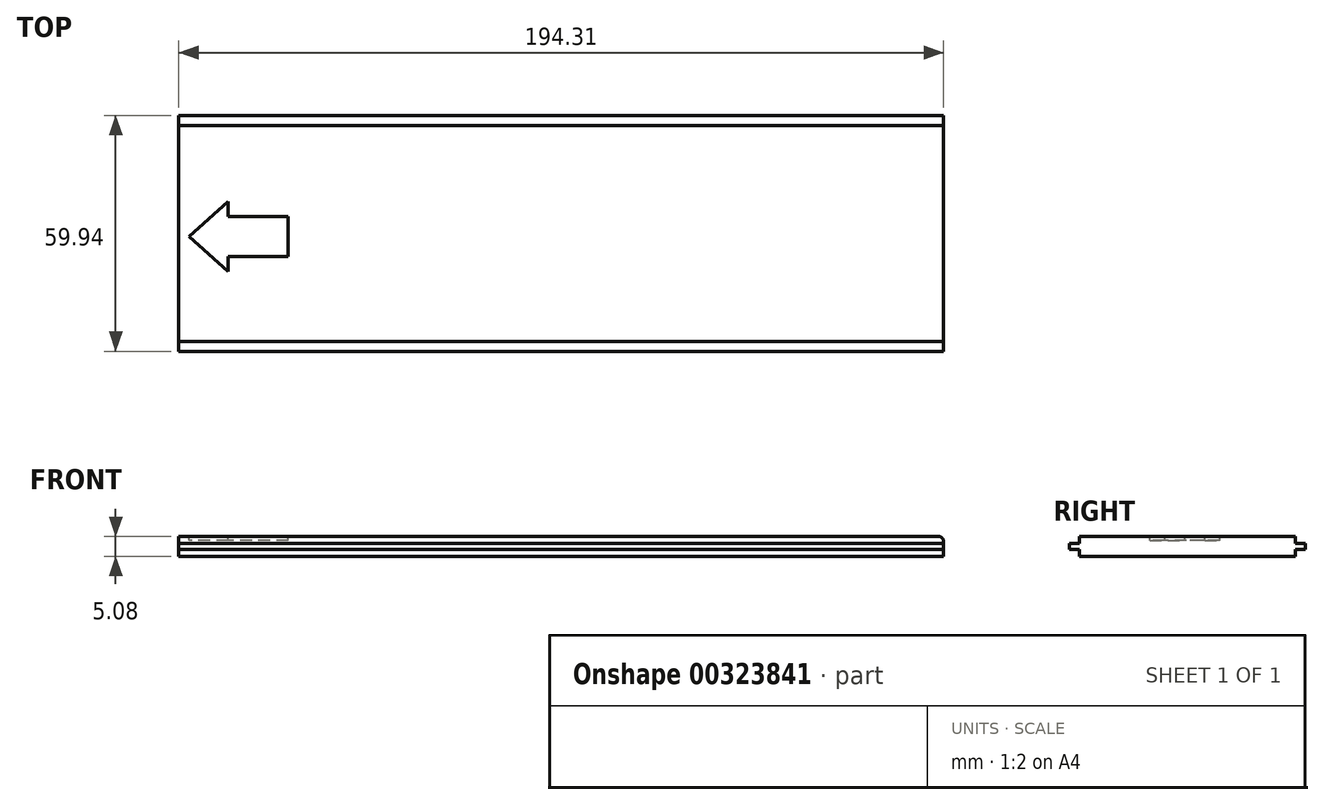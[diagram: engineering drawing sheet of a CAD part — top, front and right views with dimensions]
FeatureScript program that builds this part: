
annotation { "Feature Type Name" : "Feature", "Feature Type Description" : "" }
export const myFeature = defineFeature(function(context is Context, id is Id, definition is map)
    precondition{}
    {
        {
            var Q0;
            Q0=qCreatedBy(makeId("Top.planeOp"),FACE);
            var sketch = newSketch(context, id + "F0", { "sketchPlane" : qUnion([Q0])});
            skLineSegment(sketch, "E0.bottom", {"start": v(-32.03, -26.71) * mm, "end": v(162.28, -26.71) * mm});
            skLineSegment(sketch, "E0.top", {"start": v(-32.03, 28.15) * mm, "end": v(162.28, 28.15) * mm});
            skLineSegment(sketch, "E0.left", {"start": v(-32.03, -26.71) * mm, "end": v(-32.03, 28.15) * mm});
            skLineSegment(sketch, "E0.right", {"start": v(162.28, -26.71) * mm, "end": v(162.28, 28.15) * mm});
            skSolve(sketch);
        }
        {
            var Q0;
            Q0=makeQuery(id+"F0.imprint","IMPRINT",FACE,{"disambiguationData":[TD([[makeQuery(id+"F0.imprint","IMPRINT",EDGE,{"derivedFrom":sQuery(id+"F0.wireOp",EDGE,"E0.bottom")}),1.0]])]});
            extrude(context, id + "F1", {"entities" : qUnion([Q0]), "depth" : 5.08 * mm});
        }
        {
            var Q0;
            Q0=makeQuery(id+"F1.opExtrude","SWEPT_FACE",FACE,{"disambiguationData":[OSD([sQuery(id+"F0.wireOp",EDGE,"E0.left")])]});
            var sketch = newSketch(context, id + "F2", { "sketchPlane" : qUnion([Q0])});
            skLineSegment(sketch, "E1", {"start": v(-28.15, 2.54) * mm, "end": v(-34.25, 2.54) * mm, "construction": true});
            skPoint(sketch, "E1.endSnap0", {"position": v(-28.15, 2.54) * mm});
            skLineSegment(sketch, "E2", {"start": v(-0.72, 0) * mm, "end": v(-0.72, 5.08) * mm, "construction": true});
            skLineSegment(sketch, "E3", {"start": v(-28.15, 3.3) * mm, "end": v(-30.7, 3.3) * mm});
            skLineSegment(sketch, "E4", {"start": v(-30.7, 3.3) * mm, "end": v(-30.7, 2.54) * mm});
            skLineSegment(sketch, "E5.MirrorCS", {"start": v(-28.15, 1.78) * mm, "end": v(-30.7, 1.78) * mm});
            skLineSegment(sketch, "E6.MirrorCS", {"start": v(-30.7, 1.78) * mm, "end": v(-30.7, 2.54) * mm});
            skLineSegment(sketch, "E7.MirrorCS", {"start": v(26.71, 1.78) * mm, "end": v(29.25, 1.78) * mm});
            skLineSegment(sketch, "E8.MirrorCS", {"start": v(29.25, 1.78) * mm, "end": v(29.25, 2.54) * mm});
            skLineSegment(sketch, "E9.MirrorCS", {"start": v(29.25, 3.3) * mm, "end": v(29.25, 2.54) * mm});
            skLineSegment(sketch, "E10.MirrorCS", {"start": v(26.71, 3.3) * mm, "end": v(29.25, 3.3) * mm});
            skSolve(sketch);
        }
        {
            var Q0;
            {var subQ1=sQuery(id+"F2.wireOp",EDGE,"E3");Q0=makeQuery(id+"F2.imprint","IMPRINT",FACE,{"disambiguationData":[TD([[makeQuery(id+"F2.imprint","IMPRINT",EDGE,{"derivedFrom":subQ1}),1.0]])]});}
            var Q1;
            {var subQ1=sQuery(id+"F2.wireOp",EDGE,"E7.MirrorCS");Q1=makeQuery(id+"F2.imprint","IMPRINT",FACE,{"disambiguationData":[TD([[makeQuery(id+"F2.imprint","IMPRINT",EDGE,{"derivedFrom":subQ1}),1.0]])]});}
            var Q2;
            Q2=makeQuery(id+"F1.opExtrude","SWEPT_FACE",FACE,{"disambiguationData":[OSD([sQuery(id+"F0.wireOp",EDGE,"E0.right")])]});
            extrude(context, id + "F3", {"entities" : qUnion([Q0, Q1]), "operationType" : NewBodyOperationType.ADD, "endBound" : BoundingType.UP_TO_SURFACE, "oppositeDirection" : true, "endBoundEntityFace" : qUnion([Q2]), "depth" : 25.4 * mm});
        }
        {
            var Q0;
            Q0=makeQuery(id+"F1.opExtrude","CAP_EDGE",EDGE,{"disambiguationData":[OSD([sQuery(id+"F0.wireOp",EDGE,"E0.right")])],"isStart":false});
            fillet(context, id + "F4", {"entities" : qUnion([Q0]), "radius" : 1.27 * mm, "tangentPropagation" : true, "allowEdgeOverflow" : false});
        }
        {
            var Q0;
            Q0=makeQuery(id+"F1.opExtrude","CAP_FACE",FACE,{"disambiguationData":[OSD([sQuery(id+"F0.wireOp",EDGE,"E0.bottom"),sQuery(id+"F0.wireOp",EDGE,"E0.top"),sQuery(id+"F0.wireOp",EDGE,"E0.left"),sQuery(id+"F0.wireOp",EDGE,"E0.right")])],"isStart":false});
            var sketch = newSketch(context, id + "F5", { "sketchPlane" : qUnion([Q0])});
            skLineSegment(sketch, "E11.0.0", {"start": v(-32.03, -26.71) * mm, "end": v(161, -26.71) * mm});
            skLineSegment(sketch, "E11.0.1", {"start": v(161, -26.71) * mm, "end": v(161, 28.15) * mm});
            skLineSegment(sketch, "E11.0.2", {"start": v(161, 28.15) * mm, "end": v(-32.03, 28.15) * mm});
            skLineSegment(sketch, "E11.0.3", {"start": v(-32.03, 28.15) * mm, "end": v(-32.03, -26.71) * mm});
            skLineSegment(sketch, "E12", {"start": v(-29.45, 0) * mm, "end": v(-4.24, 0) * mm, "construction": true});
            skLineSegment(sketch, "E13", {"start": v(-4.24, 0) * mm, "end": v(-4.24, -5.08) * mm});
            skLineSegment(sketch, "E14", {"start": v(-4.24, -5.08) * mm, "end": v(-19.48, -5.08) * mm});
            skLineSegment(sketch, "E15", {"start": v(-19.48, -5.08) * mm, "end": v(-19.48, -8.9) * mm});
            skLineSegment(sketch, "E16", {"start": v(-19.48, -8.9) * mm, "end": v(-29.45, 0) * mm});
            skLineSegment(sketch, "E17.MirrorCS", {"start": v(-19.48, 8.9) * mm, "end": v(-29.45, 0) * mm});
            skLineSegment(sketch, "E18.MirrorCS", {"start": v(-19.48, 5.08) * mm, "end": v(-19.48, 8.9) * mm});
            skLineSegment(sketch, "E19.MirrorCS", {"start": v(-4.24, 5.08) * mm, "end": v(-19.48, 5.08) * mm});
            skLineSegment(sketch, "E20.MirrorCS", {"start": v(-4.24, 0) * mm, "end": v(-4.24, 5.08) * mm});
            skSolve(sketch);
        }
        {
            var Q0;
            Q0=makeQuery(id+"F5.imprint","IMPRINT",FACE,{"disambiguationData":[TD([[makeQuery(id+"F5.imprint","IMPRINT",EDGE,{"derivedFrom":sQuery(id+"F5.wireOp",EDGE,"E13")}),-1.0]])]});
            extrude(context, id + "F6", {"entities" : qUnion([Q0]), "operationType" : NewBodyOperationType.REMOVE, "oppositeDirection" : true, "depth" : 1.02 * mm});
        }
    });
